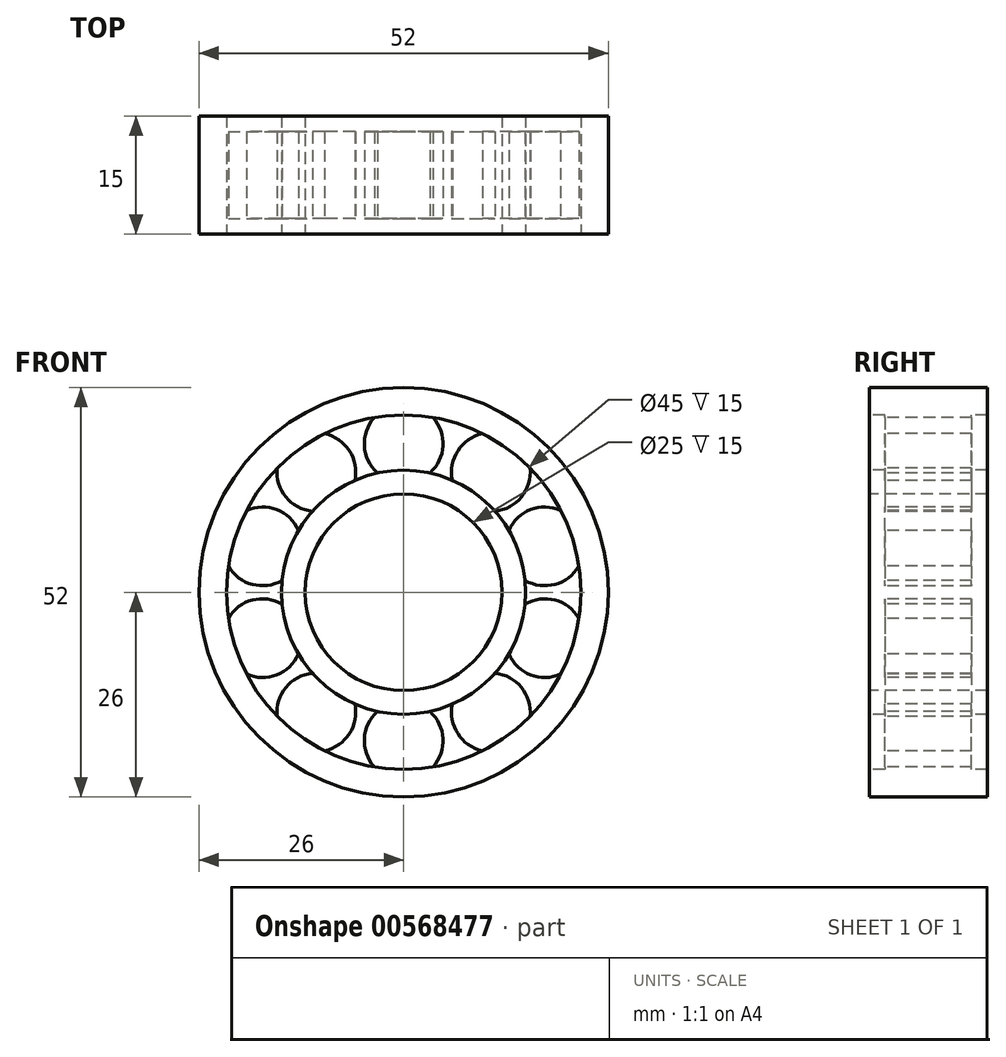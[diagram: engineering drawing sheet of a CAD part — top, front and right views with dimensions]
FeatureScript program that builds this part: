
annotation { "Feature Type Name" : "Feature", "Feature Type Description" : "" }
export const myFeature = defineFeature(function(context is Context, id is Id, definition is map)
    precondition{}
    {
        {
            var Q0;
            Q0=qCreatedBy(makeId("Front.planeOp"),FACE);
            var sketch = newSketch(context, id + "F0", { "sketchPlane" : qUnion([Q0])});
            skCircle(sketch, "E0", {"center": v(0, 0) * mm, "radius": 22.5 * mm});
            skCircle(sketch, "E1", {"center": v(0, 0) * mm, "radius": 26 * mm});
            skCircle(sketch, "E2", {"center": v(0, 0) * mm, "radius": 12.5 * mm});
            skCircle(sketch, "E3", {"center": v(0, 0) * mm, "radius": 15.5 * mm});
            skSolve(sketch);
        }
        {
            var Q0;
            Q0 = qSketchRegion(id + "F0", true);
            var Q1;
            Q1=makeQuery(id+"F0.imprint","IMPRINT",FACE,{"disambiguationData":[TD([[makeQuery(id+"F0.imprint","IMPRINT",EDGE,{"derivedFrom":sQuery(id+"F0.wireOp",EDGE,"E2")}),-1.0]])]});
            extrude(context, id + "F1", {"entities" : qUnion([Q0, Q1]), "oppositeDirection" : true, "depth" : 15 * mm, "offsetDistance" : 25.4 * mm});
        }
        {
            var Q0;
            Q0=qCreatedBy(makeId("Front.planeOp"),FACE);
            cPlane(context, id + "F2", {"entities" : qUnion([Q0]), "cplaneType" : CPlaneType.OFFSET, "offset" : 2 * mm, "oppositeDirection" : true, "width" : 152.4 * mm, "height" : 152.4 * mm});
        }
        {
            var Q0;
            Q0=qCreatedBy(id+"F2.planeOp",FACE);
            var sketch = newSketch(context, id + "F3", { "sketchPlane" : qUnion([Q0])});
            skCircle(sketch, "E4", {"center": v(0, 18.86) * mm, "radius": 5 * mm});
            skCircle(sketch, "E5.1.0", {"center": v(-11.08, 15.26) * mm, "radius": 5 * mm});
            skCircle(sketch, "E5.2.0", {"center": v(-17.94, 5.83) * mm, "radius": 5 * mm});
            skCircle(sketch, "E5.3.0", {"center": v(-17.94, -5.83) * mm, "radius": 5 * mm});
            skCircle(sketch, "E5.4.0", {"center": v(-11.08, -15.26) * mm, "radius": 5 * mm});
            skCircle(sketch, "E5.5.0", {"center": v(0, -18.86) * mm, "radius": 5 * mm});
            skCircle(sketch, "E5.6.0", {"center": v(11.08, -15.26) * mm, "radius": 5 * mm});
            skCircle(sketch, "E5.7.0", {"center": v(17.94, -5.83) * mm, "radius": 5 * mm});
            skCircle(sketch, "E5.8.0", {"center": v(17.94, 5.83) * mm, "radius": 5 * mm});
            skCircle(sketch, "E5.9.0", {"center": v(11.08, 15.26) * mm, "radius": 5 * mm});
            skPoint(sketch, "E5.center", {"position": v(0, 0) * mm});
            skSolve(sketch);
        }
        {
            var Q0;
            Q0=makeQuery(id+"F3.imprint","IMPRINT",FACE,{"disambiguationData":[TD([[makeQuery(id+"F3.imprint","IMPRINT",EDGE,{"derivedFrom":sQuery(id+"F3.wireOp",EDGE,"E5.9.0")}),1.0]])]});
            var Q1;
            Q1=makeQuery(id+"F3.imprint","IMPRINT",FACE,{"disambiguationData":[TD([[makeQuery(id+"F3.imprint","IMPRINT",EDGE,{"derivedFrom":sQuery(id+"F3.wireOp",EDGE,"E5.8.0")}),1.0]])]});
            var Q2;
            Q2=makeQuery(id+"F3.imprint","IMPRINT",FACE,{"disambiguationData":[TD([[makeQuery(id+"F3.imprint","IMPRINT",EDGE,{"derivedFrom":sQuery(id+"F3.wireOp",EDGE,"E5.7.0")}),1.0]])]});
            var Q3;
            Q3=makeQuery(id+"F3.imprint","IMPRINT",FACE,{"disambiguationData":[TD([[makeQuery(id+"F3.imprint","IMPRINT",EDGE,{"derivedFrom":sQuery(id+"F3.wireOp",EDGE,"E5.6.0")}),1.0]])]});
            var Q4;
            Q4=makeQuery(id+"F3.imprint","IMPRINT",FACE,{"disambiguationData":[TD([[makeQuery(id+"F3.imprint","IMPRINT",EDGE,{"derivedFrom":sQuery(id+"F3.wireOp",EDGE,"E5.5.0")}),1.0]])]});
            var Q5;
            Q5=makeQuery(id+"F3.imprint","IMPRINT",FACE,{"disambiguationData":[TD([[makeQuery(id+"F3.imprint","IMPRINT",EDGE,{"derivedFrom":sQuery(id+"F3.wireOp",EDGE,"E5.4.0")}),1.0]])]});
            var Q6;
            Q6=makeQuery(id+"F3.imprint","IMPRINT",FACE,{"disambiguationData":[TD([[makeQuery(id+"F3.imprint","IMPRINT",EDGE,{"derivedFrom":sQuery(id+"F3.wireOp",EDGE,"E5.3.0")}),1.0]])]});
            var Q7;
            Q7=makeQuery(id+"F3.imprint","IMPRINT",FACE,{"disambiguationData":[TD([[makeQuery(id+"F3.imprint","IMPRINT",EDGE,{"derivedFrom":sQuery(id+"F3.wireOp",EDGE,"E5.1.0")}),1.0]])]});
            var Q8;
            Q8=makeQuery(id+"F3.imprint","IMPRINT",FACE,{"disambiguationData":[TD([[makeQuery(id+"F3.imprint","IMPRINT",EDGE,{"derivedFrom":sQuery(id+"F3.wireOp",EDGE,"E4")}),1.0]])]});
            var Q9;
            Q9=makeQuery(id+"F3.imprint","IMPRINT",FACE,{"disambiguationData":[TD([[makeQuery(id+"F3.imprint","IMPRINT",EDGE,{"derivedFrom":sQuery(id+"F3.wireOp",EDGE,"E5.2.0")}),1.0]])]});
            extrude(context, id + "F4", {"entities" : qUnion([Q0, Q1, Q2, Q3, Q4, Q5, Q6, Q7, Q8, Q9]), "operationType" : NewBodyOperationType.ADD, "oppositeDirection" : true, "depth" : 11 * mm, "offsetDistance" : 25.4 * mm});
        }
    });
